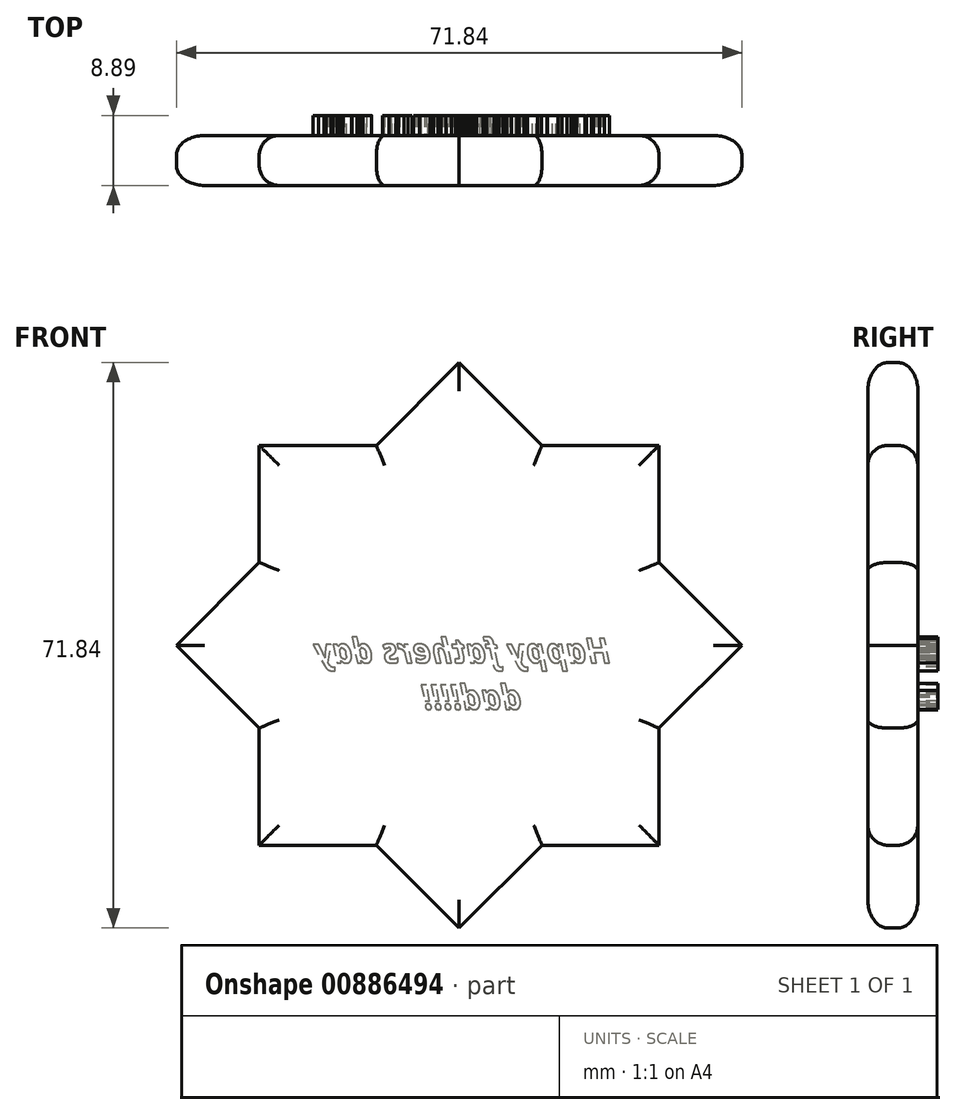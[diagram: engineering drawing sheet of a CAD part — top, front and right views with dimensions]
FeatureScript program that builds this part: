
annotation { "Feature Type Name" : "Feature", "Feature Type Description" : "" }
export const myFeature = defineFeature(function(context is Context, id is Id, definition is map)
    precondition{}
    {
        {
            var Q0;
            Q0=qCreatedBy(makeId("Front.planeOp"),FACE);
            var sketch = newSketch(context, id + "F0", { "sketchPlane" : qUnion([Q0])});
            skLineSegment(sketch, "E0.bottom", {"start": v(-25.4, -25.4) * mm, "end": v(25.4, -25.4) * mm});
            skLineSegment(sketch, "E0.top", {"start": v(-25.4, 25.4) * mm, "end": v(25.4, 25.4) * mm});
            skLineSegment(sketch, "E0.left", {"start": v(-25.4, -25.4) * mm, "end": v(-25.4, 25.4) * mm});
            skLineSegment(sketch, "E0.right", {"start": v(25.4, -25.4) * mm, "end": v(25.4, 25.4) * mm});
            skLineSegment(sketch, "E1.bottom", {"start": v(-35.92, 0) * mm, "end": v(0, -35.92) * mm});
            skLineSegment(sketch, "E1.top", {"start": v(0, 35.92) * mm, "end": v(35.92, 0) * mm});
            skLineSegment(sketch, "E1.left", {"start": v(-35.92, 0) * mm, "end": v(0, 35.92) * mm});
            skLineSegment(sketch, "E1.right", {"start": v(0, -35.92) * mm, "end": v(35.92, 0) * mm});
            skLineSegment(sketch, "E2", {"start": v(39.45, 17) * mm, "end": v(66.82, 29.93) * mm});
            skLineSegment(sketch, "E3", {"start": v(32.53, 25.12) * mm, "end": v(53.89, 46.47) * mm});
            skLineSegment(sketch, "E4", {"start": v(23.5, 31.43) * mm, "end": v(40.35, 56.7) * mm});
            skLineSegment(sketch, "E5", {"start": v(13.28, 35.92) * mm, "end": v(25.91, 63.02) * mm});
            skLineSegment(sketch, "E6", {"start": v(0, 40.76) * mm, "end": v(0, 66.32) * mm});
            skLineSegment(sketch, "E7", {"start": v(-9.28, 35.92) * mm, "end": v(-25.4, 66.32) * mm});
            skLineSegment(sketch, "E8", {"start": v(-18.9, 33.54) * mm, "end": v(-40.56, 61.81) * mm});
            skLineSegment(sketch, "E9", {"start": v(-33.94, 22.7) * mm, "end": v(-64.62, 36.85) * mm});
            skLineSegment(sketch, "E10", {"start": v(-35.45, 14.59) * mm, "end": v(-67.03, 18.8) * mm});
            skLineSegment(sketch, "E11", {"start": v(6.66, 37.15) * mm, "end": v(11.48, 66.32) * mm});
            skLineSegment(sketch, "E12", {"start": v(-28.83, 29.63) * mm, "end": v(-52.9, 53.7) * mm});
            skSolve(sketch);
        }
        {
            var Q0;
            Q0 = qSketchRegion(id + "F0", true);
            extrude(context, id + "F1", {"entities" : qUnion([Q0]), "depth" : 6.35 * mm, "offsetDistance" : 25.4 * mm});
        }
        {
            var Q0;
            Q0=makeQuery(id+"F1.opExtrude","CAP_FACE",FACE,{"disambiguationData":[OSD([sQuery(id+"F0.wireOp",EDGE,"E0.bottom"),sQuery(id+"F0.wireOp",EDGE,"E0.top"),sQuery(id+"F0.wireOp",EDGE,"E0.left"),sQuery(id+"F0.wireOp",EDGE,"E0.right"),sQuery(id+"F0.wireOp",EDGE,"E1.bottom"),sQuery(id+"F0.wireOp",EDGE,"E1.top"),sQuery(id+"F0.wireOp",EDGE,"E1.left"),sQuery(id+"F0.wireOp",EDGE,"E1.right")])],"isStart":true});
            var sketch = newSketch(context, id + "F2", { "sketchPlane" : qUnion([Q0])});
            skText(sketch, "E13", { "text": "Happy fathers day\n          dad!!!!\n", "fontName": "OpenSans-BoldItalic.ttf"});
            const initialGuessF2  = {"E13": [-0.01923, -0.00223, 1, 0, 0.00312]};
            skSetInitialGuess(sketch, initialGuessF2);
            skSolve(sketch);
        }
        {
            var Q0;
            Q0 = qSketchRegion(id + "F2", true);
            extrude(context, id + "F3", {"entities" : qUnion([Q0]), "operationType" : NewBodyOperationType.ADD, "depth" : 2.54 * mm, "offsetDistance" : 25.4 * mm});
        }
        {
            var Q0;
            {var subQ0=sQuery(id+"F0.wireOp",EDGE,"E0.top");Q0=makeQuery(id+"F1.opExtrude","CAP_EDGE",EDGE,{"disambiguationData":[OSD([subQ0]),TDD([makeQuery(id+"F0.imprint","IMPRINT",EDGE,{"disambiguationData":[TD([[makeQuery(id+"F0.imprint","INTERSECT",VERTEX,{"derivedFrom":[subQ0,sQuery(id+"F0.wireOp",EDGE,"E0.right")]}),1.0]])],"derivedFrom":subQ0})])],"isStart":true});}
            var Q1;
            {var subQ0=sQuery(id+"F0.wireOp",EDGE,"E1.top");Q1=makeQuery(id+"F1.opExtrude","CAP_EDGE",EDGE,{"disambiguationData":[OSD([subQ0]),TDD([makeQuery(id+"F0.imprint","IMPRINT",EDGE,{"disambiguationData":[TD([[makeQuery(id+"F0.imprint","INTERSECT",VERTEX,{"derivedFrom":[subQ0,sQuery(id+"F0.wireOp",EDGE,"E1.left")]}),-1.0]])],"derivedFrom":subQ0})])],"isStart":true});}
            var Q2;
            {var subQ0=sQuery(id+"F0.wireOp",EDGE,"E1.left");Q2=makeQuery(id+"F1.opExtrude","CAP_EDGE",EDGE,{"disambiguationData":[OSD([subQ0]),TDD([makeQuery(id+"F0.imprint","IMPRINT",EDGE,{"disambiguationData":[TD([[makeQuery(id+"F0.imprint","INTERSECT",VERTEX,{"derivedFrom":[sQuery(id+"F0.wireOp",EDGE,"E1.top"),subQ0]}),1.0]])],"derivedFrom":subQ0})])],"isStart":true});}
            var Q3;
            {var subQ0=sQuery(id+"F0.wireOp",EDGE,"E0.top");Q3=makeQuery(id+"F1.opExtrude","CAP_EDGE",EDGE,{"disambiguationData":[OSD([subQ0]),TDD([makeQuery(id+"F0.imprint","IMPRINT",EDGE,{"disambiguationData":[TD([[makeQuery(id+"F0.imprint","INTERSECT",VERTEX,{"derivedFrom":[subQ0,sQuery(id+"F0.wireOp",EDGE,"E0.left")]}),-1.0]])],"derivedFrom":subQ0})])],"isStart":true});}
            var Q4;
            {var subQ0=sQuery(id+"F0.wireOp",EDGE,"E0.left");Q4=makeQuery(id+"F1.opExtrude","CAP_EDGE",EDGE,{"disambiguationData":[OSD([subQ0]),TDD([makeQuery(id+"F0.imprint","IMPRINT",EDGE,{"disambiguationData":[TD([[makeQuery(id+"F0.imprint","INTERSECT",VERTEX,{"derivedFrom":[sQuery(id+"F0.wireOp",EDGE,"E0.top"),subQ0]}),1.0]])],"derivedFrom":subQ0})])],"isStart":true});}
            var Q5;
            {var subQ0=sQuery(id+"F0.wireOp",EDGE,"E1.left");Q5=makeQuery(id+"F1.opExtrude","CAP_EDGE",EDGE,{"disambiguationData":[OSD([subQ0]),TDD([makeQuery(id+"F0.imprint","IMPRINT",EDGE,{"disambiguationData":[TD([[makeQuery(id+"F0.imprint","INTERSECT",VERTEX,{"derivedFrom":[sQuery(id+"F0.wireOp",EDGE,"E1.bottom"),subQ0]}),-1.0]])],"derivedFrom":subQ0})])],"isStart":true});}
            var Q6;
            {var subQ0=sQuery(id+"F0.wireOp",EDGE,"E1.bottom");Q6=makeQuery(id+"F1.opExtrude","CAP_EDGE",EDGE,{"disambiguationData":[OSD([subQ0]),TDD([makeQuery(id+"F0.imprint","IMPRINT",EDGE,{"disambiguationData":[TD([[makeQuery(id+"F0.imprint","INTERSECT",VERTEX,{"derivedFrom":[subQ0,sQuery(id+"F0.wireOp",EDGE,"E1.left")]}),-1.0]])],"derivedFrom":subQ0})])],"isStart":true});}
            var Q7;
            {var subQ0=sQuery(id+"F0.wireOp",EDGE,"E0.left");Q7=makeQuery(id+"F1.opExtrude","CAP_EDGE",EDGE,{"disambiguationData":[OSD([subQ0]),TDD([makeQuery(id+"F0.imprint","IMPRINT",EDGE,{"disambiguationData":[TD([[makeQuery(id+"F0.imprint","INTERSECT",VERTEX,{"derivedFrom":[sQuery(id+"F0.wireOp",EDGE,"E0.bottom"),subQ0]}),-1.0]])],"derivedFrom":subQ0})])],"isStart":true});}
            var Q8;
            {var subQ0=sQuery(id+"F0.wireOp",EDGE,"E0.bottom");Q8=makeQuery(id+"F1.opExtrude","CAP_EDGE",EDGE,{"disambiguationData":[OSD([subQ0]),TDD([makeQuery(id+"F0.imprint","IMPRINT",EDGE,{"disambiguationData":[TD([[makeQuery(id+"F0.imprint","INTERSECT",VERTEX,{"derivedFrom":[subQ0,sQuery(id+"F0.wireOp",EDGE,"E0.left")]}),-1.0]])],"derivedFrom":subQ0})])],"isStart":true});}
            var Q9;
            {var subQ0=sQuery(id+"F0.wireOp",EDGE,"E1.bottom");Q9=makeQuery(id+"F1.opExtrude","CAP_EDGE",EDGE,{"disambiguationData":[OSD([subQ0]),TDD([makeQuery(id+"F0.imprint","IMPRINT",EDGE,{"disambiguationData":[TD([[makeQuery(id+"F0.imprint","INTERSECT",VERTEX,{"derivedFrom":[subQ0,sQuery(id+"F0.wireOp",EDGE,"E1.right")]}),1.0]])],"derivedFrom":subQ0})])],"isStart":true});}
            var Q10;
            {var subQ0=sQuery(id+"F0.wireOp",EDGE,"E1.right");Q10=makeQuery(id+"F1.opExtrude","CAP_EDGE",EDGE,{"disambiguationData":[OSD([subQ0]),TDD([makeQuery(id+"F0.imprint","IMPRINT",EDGE,{"disambiguationData":[TD([[makeQuery(id+"F0.imprint","INTERSECT",VERTEX,{"derivedFrom":[sQuery(id+"F0.wireOp",EDGE,"E1.bottom"),subQ0]}),-1.0]])],"derivedFrom":subQ0})])],"isStart":true});}
            var Q11;
            {var subQ0=sQuery(id+"F0.wireOp",EDGE,"E0.bottom");Q11=makeQuery(id+"F1.opExtrude","CAP_EDGE",EDGE,{"disambiguationData":[OSD([subQ0]),TDD([makeQuery(id+"F0.imprint","IMPRINT",EDGE,{"disambiguationData":[TD([[makeQuery(id+"F0.imprint","INTERSECT",VERTEX,{"derivedFrom":[subQ0,sQuery(id+"F0.wireOp",EDGE,"E0.right")]}),1.0]])],"derivedFrom":subQ0})])],"isStart":true});}
            var Q12;
            {var subQ0=sQuery(id+"F0.wireOp",EDGE,"E0.right");Q12=makeQuery(id+"F1.opExtrude","CAP_EDGE",EDGE,{"disambiguationData":[OSD([subQ0]),TDD([makeQuery(id+"F0.imprint","IMPRINT",EDGE,{"disambiguationData":[TD([[makeQuery(id+"F0.imprint","INTERSECT",VERTEX,{"derivedFrom":[sQuery(id+"F0.wireOp",EDGE,"E0.bottom"),subQ0]}),-1.0]])],"derivedFrom":subQ0})])],"isStart":true});}
            var Q13;
            {var subQ0=sQuery(id+"F0.wireOp",EDGE,"E1.right");Q13=makeQuery(id+"F1.opExtrude","CAP_EDGE",EDGE,{"disambiguationData":[OSD([subQ0]),TDD([makeQuery(id+"F0.imprint","IMPRINT",EDGE,{"disambiguationData":[TD([[makeQuery(id+"F0.imprint","INTERSECT",VERTEX,{"derivedFrom":[sQuery(id+"F0.wireOp",EDGE,"E1.top"),subQ0]}),1.0]])],"derivedFrom":subQ0})])],"isStart":true});}
            var Q14;
            {var subQ0=sQuery(id+"F0.wireOp",EDGE,"E1.top");Q14=makeQuery(id+"F1.opExtrude","CAP_EDGE",EDGE,{"disambiguationData":[OSD([subQ0]),TDD([makeQuery(id+"F0.imprint","IMPRINT",EDGE,{"disambiguationData":[TD([[makeQuery(id+"F0.imprint","INTERSECT",VERTEX,{"derivedFrom":[subQ0,sQuery(id+"F0.wireOp",EDGE,"E1.right")]}),1.0]])],"derivedFrom":subQ0})])],"isStart":true});}
            var Q15;
            {var subQ0=sQuery(id+"F0.wireOp",EDGE,"E0.right");Q15=makeQuery(id+"F1.opExtrude","CAP_EDGE",EDGE,{"disambiguationData":[OSD([subQ0]),TDD([makeQuery(id+"F0.imprint","IMPRINT",EDGE,{"disambiguationData":[TD([[makeQuery(id+"F0.imprint","INTERSECT",VERTEX,{"derivedFrom":[sQuery(id+"F0.wireOp",EDGE,"E0.top"),subQ0]}),1.0]])],"derivedFrom":subQ0})])],"isStart":true});}
            var Q16;
            {var subQ0=sQuery(id+"F0.wireOp",EDGE,"E1.left");Q16=makeQuery(id+"F1.opExtrude","CAP_EDGE",EDGE,{"disambiguationData":[OSD([subQ0]),TDD([makeQuery(id+"F0.imprint","IMPRINT",EDGE,{"disambiguationData":[TD([[makeQuery(id+"F0.imprint","INTERSECT",VERTEX,{"derivedFrom":[sQuery(id+"F0.wireOp",EDGE,"E1.bottom"),subQ0]}),-1.0]])],"derivedFrom":subQ0})])],"isStart":false});}
            var Q17;
            Q17=makeQuery(id+"F1.opExtrude","CAP_FACE",FACE,{"disambiguationData":[OSD([sQuery(id+"F0.wireOp",EDGE,"E0.bottom"),sQuery(id+"F0.wireOp",EDGE,"E0.top"),sQuery(id+"F0.wireOp",EDGE,"E0.left"),sQuery(id+"F0.wireOp",EDGE,"E0.right"),sQuery(id+"F0.wireOp",EDGE,"E1.bottom"),sQuery(id+"F0.wireOp",EDGE,"E1.top"),sQuery(id+"F0.wireOp",EDGE,"E1.left"),sQuery(id+"F0.wireOp",EDGE,"E1.right")])],"isStart":false});
            fillet(context, id + "F4", {"entities" : qUnion([Q0, Q1, Q2, Q3, Q4, Q5, Q6, Q7, Q8, Q9, Q10, Q11, Q12, Q13, Q14, Q15, Q16, Q17]), "radius" : 2.54 * mm, "tangentPropagation" : true, "allowEdgeOverflow" : false});
        }
        {
            var Q0;
            Q0=sQuery(id+"F0.wireOp",EDGE,"E2");
            var Q1;
            Q1=sQuery(id+"F0.wireOp",EDGE,"E3");
            var Q2;
            Q2=sQuery(id+"F0.wireOp",EDGE,"E4");
            var Q3;
            Q3=sQuery(id+"F0.wireOp",EDGE,"E5");
            var Q4;
            Q4=sQuery(id+"F0.wireOp",EDGE,"E11");
            var Q5;
            Q5=sQuery(id+"F0.wireOp",EDGE,"E6");
            var Q6;
            Q6=sQuery(id+"F0.wireOp",EDGE,"E7");
            var Q7;
            Q7=sQuery(id+"F0.wireOp",EDGE,"E8");
            var Q8;
            Q8=sQuery(id+"F0.wireOp",EDGE,"E12");
            var Q9;
            Q9=sQuery(id+"F0.wireOp",EDGE,"E9");
            var Q10;
            Q10=sQuery(id+"F0.wireOp",EDGE,"E10");
            extrude(context, id + "F5", {"bodyType" : ToolBodyType.SURFACE, "surfaceEntities" : qUnion([Q0, Q1, Q2, Q3, Q4, Q5, Q6, Q7, Q8, Q9, Q10]), "depth" : 6.35 * mm, "offsetDistance" : 25.4 * mm});
        }
    });
